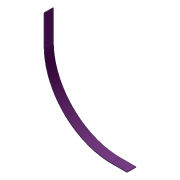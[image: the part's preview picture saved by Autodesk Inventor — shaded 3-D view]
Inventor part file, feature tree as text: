
AUTODESK INVENTOR PART (.ipt)
format: ipt  version: 2012 (Build 160160000, 160)  size: 78,336 bytes
history: native  units: in
note: dims shown in document units (in); Inventor stores cm internally (conversion verified against a paired STEP export)
features: extrude x1, sketch x1
ambient origin geometry x8: Origin, YZ Plane, XZ Plane, XY Plane, X Axis, Y Axis, Z Axis, Center Point
bodies: Solid1 (feature_tree)
feature tree (2):
  extrude  "Extrusion1"  Depth=0.125in
  sketch  "Sketch1"  dims[d0=29.5in d2=0.125in d5=2.0in d6=0.0in]
